# Revit family: Camera-Security-Panasonic-Super_Dynamic-Super_Resolution-Network-Fixed_Dome-WV-S1132SeriesY
name_source: partatom
category: Security Devices
revit_build: Autodesk Revit 2013 (Build: 20130531_2115(x64)
units: mm (PartAtom-declared; Revit-internal decimal feet)

## types (4) — shared parameters
Alarm Input Or Output Specification = ALARM IN 1 (DAY/NIGHT IN, Auto time adjustment) (x1), ALARM IN 2 (ALARM OUT) (x1), ALARM IN 3 (AUX OUT) (x1)
Angle Of View = Lens Dependent
Audio In = Yes
Audio Out = Yes
Auto Back Focus = Yes
Communication Ports = 10Base-T / 100Base-TX, RJ45 connector
Date Last Modified = December, 14, 2016
Day Or Night = Yes
Depth = 5.748 "
Equipment Abbreviation = SC
Family Version = 1.0.0
Has POE = Yes
Height = 2.244 "
IP Or Analog = IP
Indoor Or Outdoor = Indoor
Manufacturer = Panasonic
Model Disclaimer = Contact Panasonic for more information
Mounting Positions = Mount Dependent
Operational Humidity = 10 to 90 % (no condensation)
Operational Temperature = -10 °C to +50 °C (14 °F to 122 °F)
Product Documentation Link = http://ssbu-t.psn-web.net
Product Material = Paint - Panasonic - Sail White
Product Page URL = http://security.panasonic.com
Provide Feedback = https://www.surveymonkey.com
Regulatory Compliance = UL UL60950-1, C-UL CAN/CSA C22.2 No.60950-1, CE, IEC60950-1 FCC Part15 ClassA, ICES003 ClassA, EN55022 ClassB, EN55024
Storage Temperature = -10 °C to +50 °C (14 °F to 122 °F)
URL = http://security.panasonic.com
Vandal Resistant = No
Voltage DC = 12 V
Weight = 0.77 lb
Wide Dynamic Range = Yes
Width = 2.953 "
z Front Radius = 0.787 "

## per-type parameters (varying)
| type | Description | Minimum Illumination | Model | Part Description | Part Number | z Type |
| Full HD, WV-S1132 | Security Camera, Network, Super Dynamic, Full HD, iA, Smart Facial Coding | 0.010 lx | WV-S1132 | Security Camera, Network, Super Dynamic, Full HD, iA, Smart Facial Coding | WV-S1132 | 4 |
| HD, WV-S1111 | Security Camera, Network, Super Dynamic, HD, iA, Smart Facial Coding | 0.007 lx | WV-S1111 | Security Camera, Network, Super Dynamic, HD, iA, Smart Facial Coding | WV-S1111 | 5 |
| Full HD, WV-S1131 | Security Camera, Network, Super Dynamic, Full HD, iA, Smart Facial Coding | 0.010 lx | WV-S1131 | Security Camera, Network, Super Dynamic, Full HD, iA, Smart Facial Coding | WV-S1131 | 3 |
| HD, WV-S1112 | Security Camera, Network, Super Dynamic, HD, iA, Smart Facial Coding | 0.007 lx | WV-S1112 | Security Camera, Network, Super Dynamic, HD, iA, Smart Facial Coding | WV-S1112 | 6 |

## geometry (parser evidence)
native form markers: Sweep x2
no freeform markers — native parametric forms only
